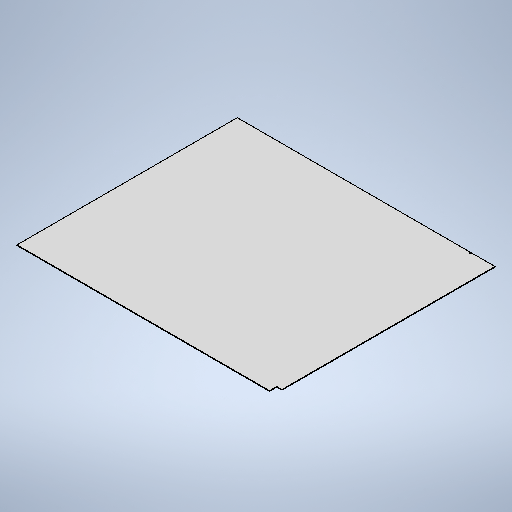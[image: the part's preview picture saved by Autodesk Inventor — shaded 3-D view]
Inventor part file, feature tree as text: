
AUTODESK INVENTOR PART (.ipt)
format: ipt  version: 2025.3 (Build 293356000, 356)  size: 292,864 bytes
history: native  units: mm
features: other x3, sketch x2, sheet_metal_op x1
ambient origin geometry x8: Origin, YZ Plane, XZ Plane, XY Plane, X Axis, Y Axis, Z Axis, Center Point
bodies: Solid1 (feature_tree)
feature tree (6):
  sheet_metal_op  "Face1"
  sketch  "Sketch1"  dims[d2=3.0mm]
  other  "Plate1"
  sketch  "Sketch5"  dims[d22=1240.0mm d23=1060.0mm d24=25.0mm d25=35.0mm d28=90.0mm d29=970.0mm d30=100.0mm d31=2.0mm d32=5.0mm d33=4.0mm d34=0.5mm d35=5.0mm d36=5.0mm d37=5.0mm d38=2.0mm d39=3.0mm d40=0.0mm]
  other  "Cut1"
  other  "Definition1"
